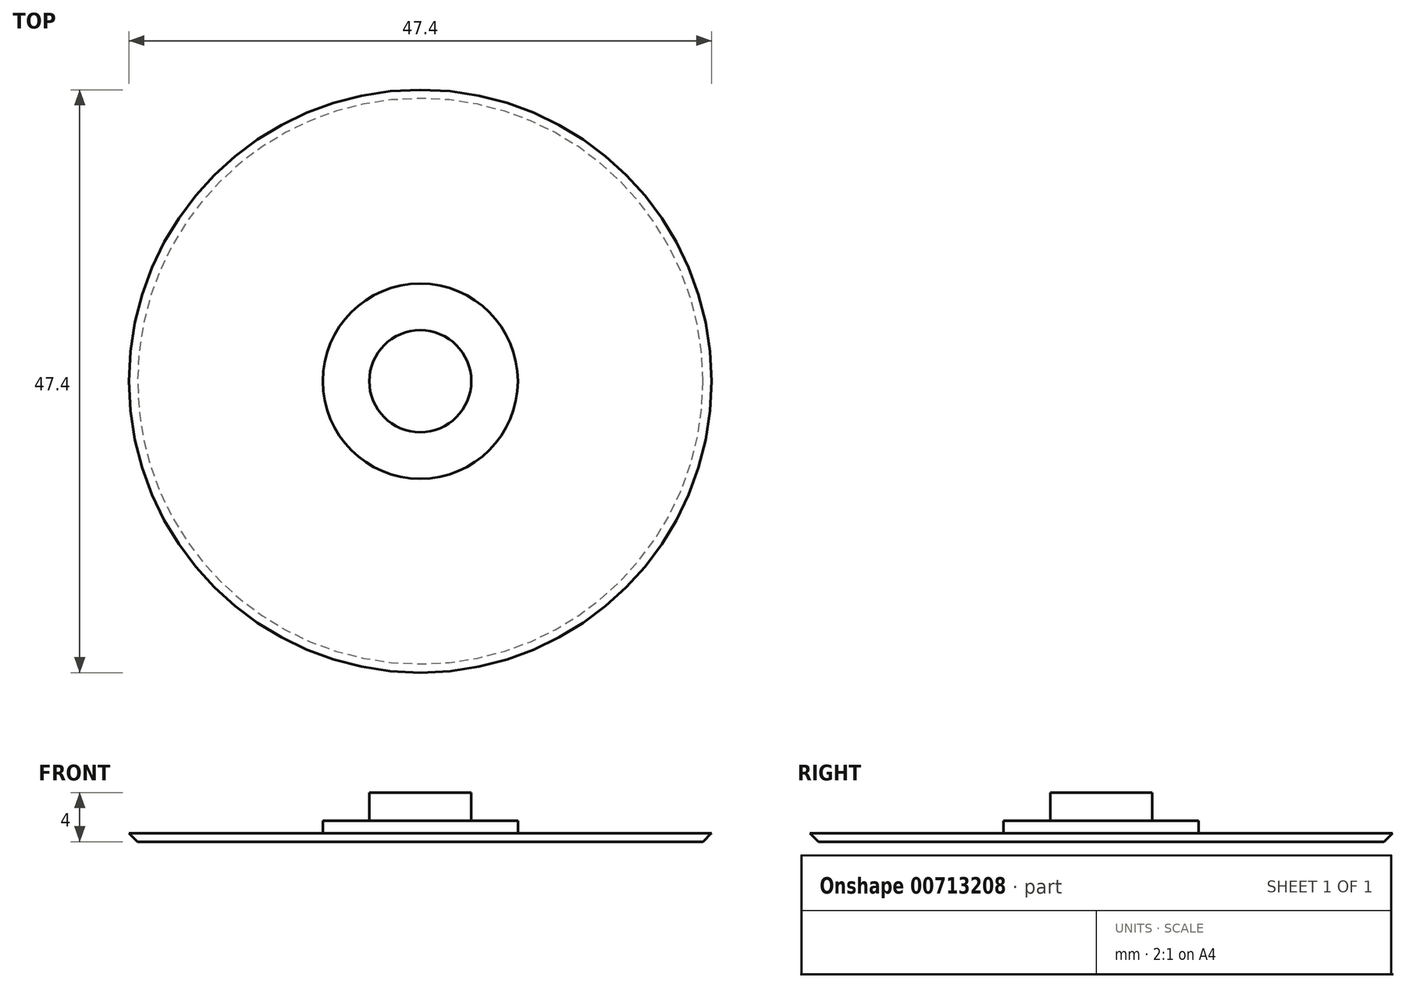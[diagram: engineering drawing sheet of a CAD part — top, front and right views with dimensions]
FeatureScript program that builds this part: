
annotation { "Feature Type Name" : "Feature", "Feature Type Description" : "" }
export const myFeature = defineFeature(function(context is Context, id is Id, definition is map)
    precondition{}
    {
        {
            var Q0;
            Q0=qCreatedBy(makeId("Top.planeOp"),FACE);
            var sketch = newSketch(context, id + "F0", { "sketchPlane" : qUnion([Q0])});
            skCircle(sketch, "E0", {"center": v(0, 0) * mm, "radius": 25 * mm});
            skCircle(sketch, "E1", {"center": v(0, 0) * mm, "radius": 7.94 * mm});
            skCircle(sketch, "E2", {"center": v(0, 0) * mm, "radius": 4.15 * mm});
            skSolve(sketch);
        }
        {
            var Q0;
            Q0=makeQuery(id+"F0.imprint","IMPRINT",FACE,{"disambiguationData":[TD([[makeQuery(id+"F0.imprint","IMPRINT",EDGE,{"derivedFrom":sQuery(id+"F0.wireOp",EDGE,"E0")}),1.0]])]});
            extrude(context, id + "F1", {"entities" : qUnion([Q0]), "depth" : .7 * mm, "offsetDistance" : 25 * mm});
        }
        {
            var Q0;
            Q0=makeQuery(id+"F0.imprint","IMPRINT",FACE,{"disambiguationData":[TD([[makeQuery(id+"F0.imprint","IMPRINT",EDGE,{"derivedFrom":sQuery(id+"F0.wireOp",EDGE,"E1")}),1.0]])]});
            extrude(context, id + "F2", {"entities" : qUnion([Q0]), "operationType" : NewBodyOperationType.ADD, "depth" : 1.7 * mm, "offsetDistance" : 25 * mm});
        }
        {
            var Q0;
            Q0=makeQuery(id+"F0.imprint","IMPRINT",FACE,{"disambiguationData":[TD([[makeQuery(id+"F0.imprint","IMPRINT",EDGE,{"derivedFrom":sQuery(id+"F0.wireOp",EDGE,"E2")}),1.0]])]});
            extrude(context, id + "F3", {"entities" : qUnion([Q0]), "operationType" : NewBodyOperationType.ADD, "depth" : 4 * mm, "offsetDistance" : 25 * mm});
        }
        {
            var Q0;
            Q0=makeQuery(id+"F1.opExtrude","CAP_EDGE",EDGE,{"disambiguationData":[OSD([sQuery(id+"F0.wireOp",EDGE,"E0")])],"isStart":true});
            chamfer(context, id + "F4", {"entities" : qUnion([Q0]), "width" : 2 * mm, "tangentPropagation" : true});
        }
    });
